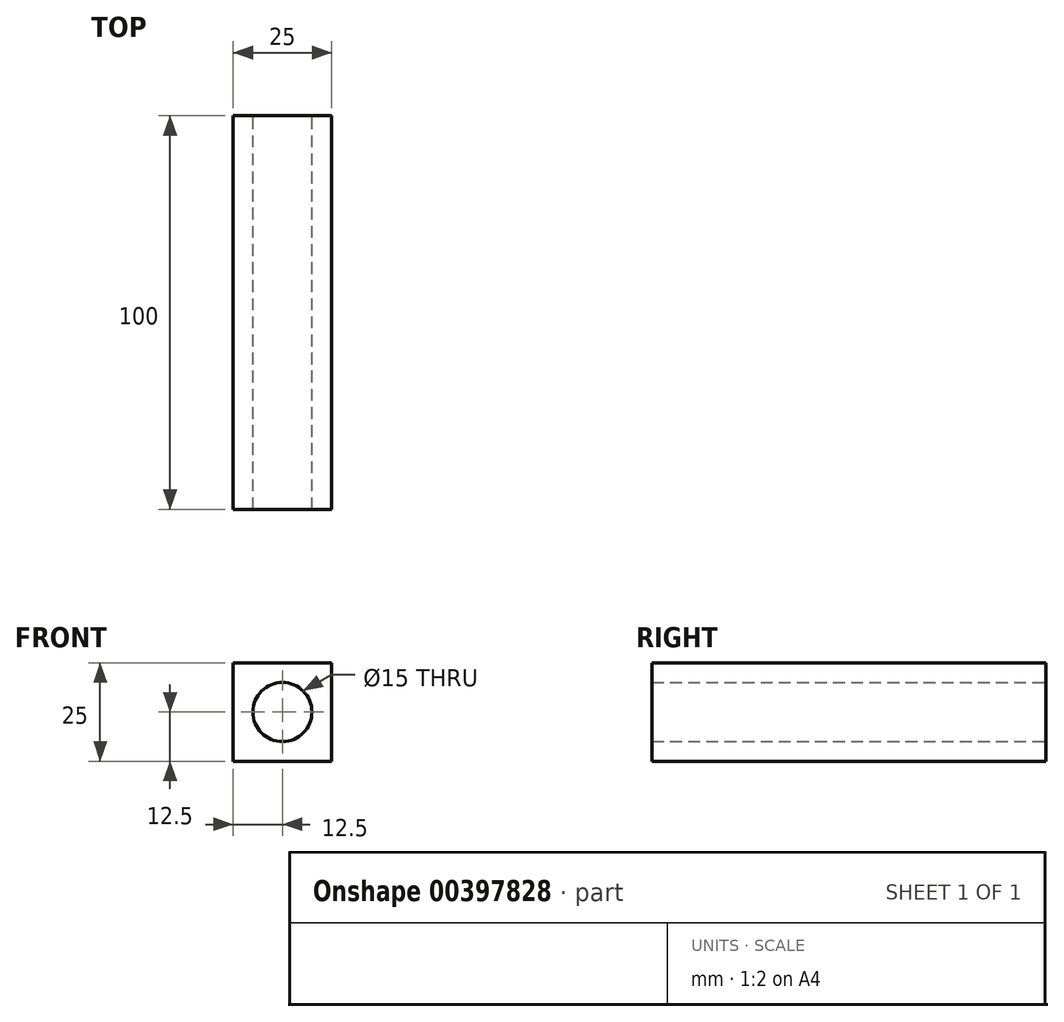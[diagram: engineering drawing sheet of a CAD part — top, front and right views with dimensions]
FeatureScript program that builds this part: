
annotation { "Feature Type Name" : "Feature", "Feature Type Description" : "" }
export const myFeature = defineFeature(function(context is Context, id is Id, definition is map)
    precondition{}
    {
        {
            var Q0;
            Q0=qCreatedBy(makeId("Front.planeOp"),FACE);
            var sketch = newSketch(context, id + "F0", { "sketchPlane" : qUnion([Q0])});
            skLineSegment(sketch, "E0.bottom", {"start": v(-12.5, 12.5) * mm, "end": v(12.5, 12.5) * mm});
            skLineSegment(sketch, "E0.top", {"start": v(-12.5, -12.5) * mm, "end": v(12.5, -12.5) * mm});
            skLineSegment(sketch, "E0.left", {"start": v(-12.5, 12.5) * mm, "end": v(-12.5, -12.5) * mm});
            skLineSegment(sketch, "E0.right", {"start": v(12.5, 12.5) * mm, "end": v(12.5, -12.5) * mm});
            skPoint(sketch, "E0.middle", {"position": v(0, 0) * mm});
            skCircle(sketch, "E1", {"center": v(0, 0) * mm, "radius": 7.5 * mm});
            skSolve(sketch);
        }
        {
            var Q0;
            Q0 = qSketchRegion(id + "F0", true);
            extrude(context, id + "F1", {"entities" : qUnion([Q0]), "depth" : 100 * mm});
        }
    });
